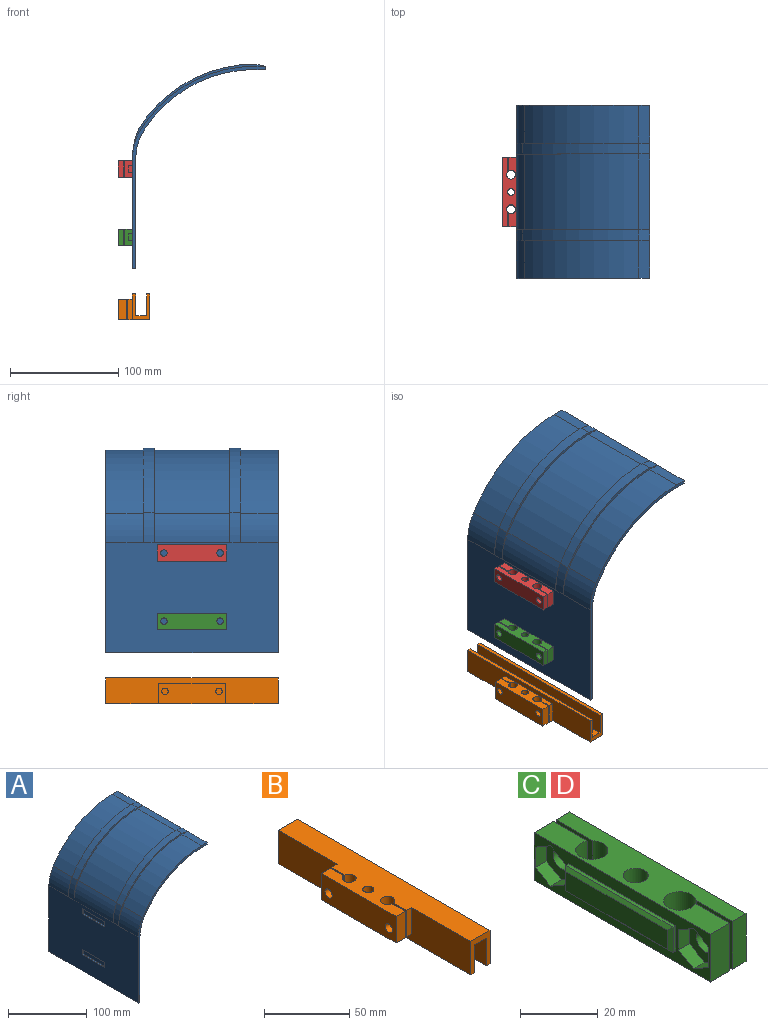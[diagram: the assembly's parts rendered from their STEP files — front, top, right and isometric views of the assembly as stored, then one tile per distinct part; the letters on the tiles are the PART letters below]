
ASSEMBLY  parts=4 mates=3
PART A: 38 faces, bbox 123.2x160x189.2 mm
  f0: plane 160x102.1mm, normal (-1,0,0), area 15695.5mm2, adj f3,f6,f12,f14,f15,f16,f20,f23
  f1: plane 35x10mm, normal (0,0,1), area 350mm2, adj f2,f9,f14,f27
  f2: cylinder r=124.43mm len=105.62mm, axis (0,1,0), area 4415.4mm2, adj f1,f3,f14,f27
  f3: cylinder r=50mm len=35mm, axis (0,1,0), area 974.6mm2, adj f0,f2,f14,f27
  f4: plane 35x10mm, normal (0,0,1), area 350mm2, adj f5,f9,f15,f22
  f5: cylinder r=124.43mm len=105.62mm, axis (0,1,0), area 4415.4mm2, adj f4,f6,f15,f22
  f6: cylinder r=50mm len=35mm, axis (0,1,0), area 974.6mm2, adj f0,f5,f15,f22
  f7: cylinder r=121.43mm len=160mm, axis (0,1,0), area 19466.7mm2, adj f8,f14,f15,f17
  f8: plane 160x10mm, normal (0,0,-1), area 1600mm2, adj f7,f9,f14,f15
  f9: plane 160x3mm, normal (1,0,0), area 480mm2, adj f1,f4,f8,f10,f14,f15,f18,f25
  f10: plane 70x10mm, normal (0,0,1), area 700mm2, adj f9,f11,f21,f26
  f11: cylinder r=124.43mm len=105.62mm, axis (0,1,0), area 8830.7mm2, adj f10,f16,f21,f26
  f12: plane 160x3mm, normal (0,0,-1), area 480mm2, adj f0,f13,f14,f15
  f13: plane 160x101.23mm, normal (1,0,0), area 16196.7mm2, adj f12,f14,f15,f17
  f14: plane 187.18x123.18mm, normal (0,-1,0), area 793.5mm2, adj f0,f1,f2,f3,f7,f8,f9,f12
  f15: plane 187.18x123.18mm, normal (0,1,0), area 793.5mm2, adj f0,f4,f5,f6,f7,f8,f9,f12
  f16: cylinder r=50mm len=70mm, axis (0,1,0), area 1949.3mm2, adj f0,f11,f21,f26
  f17: cylinder r=50mm len=160mm, axis (0,1,0), area 4550.7mm2, adj f7,f13,f14,f15
  f18: plane 10x10mm, normal (0.2,0,0.98), area 102mm2, adj f9,f19,f21,f22
  f19: cylinder r=126.43mm len=107.29mm, axis (0,1,0), area 1281.2mm2, adj f18,f20,f21,f22
  f20: cylinder r=67.31mm len=27.54mm, axis (0,1,0), area 283.7mm2, adj f0,f19,f21,f22
  f21: plane 123.18x87.09mm, normal (0,-1,0), area 283.1mm2, adj f10,f11,f16,f18,f19,f20
  f22: plane 123.18x87.09mm, normal (0,1,0), area 283.1mm2, adj f4,f5,f6,f18,f19,f20
  f23: cylinder r=67.31mm len=27.54mm, axis (0,-1,0), area 283.7mm2, adj f0,f24,f26,f27
  f24: cylinder r=126.43mm len=107.29mm, axis (0,-1,0), area 1281.2mm2, adj f23,f25,f26,f27
  f25: plane 10x10mm, normal (0.2,0,0.98), area 102mm2, adj f9,f24,f26,f27
  f26: plane 123.18x87.09mm, normal (0,1,0), area 283.1mm2, adj f10,f11,f16,f23,f24,f25
  f27: plane 123.18x87.09mm, normal (0,-1,0), area 283.1mm2, adj f1,f2,f3,f23,f24,f25
  f28: plane 40x2mm, normal (0,0,-1), area 80mm2, adj f0,f29,f31,f32
  f29: plane 8x2mm, normal (0,-1,0), area 16mm2, adj f0,f28,f30,f32
  f30: plane 40x2mm, normal (0,0,1), area 80mm2, adj f0,f29,f31,f32
  f31: plane 8x2mm, normal (0,1,0), area 16mm2, adj f0,f28,f30,f32
  f32: plane 40x8mm, normal (-1,0,0), area 320mm2, adj f28,f29,f30,f31
  f33: plane 8x2mm, normal (0,-1,0), area 16mm2, adj f0,f34,f36,f37
  f34: plane 40x2mm, normal (0,0,1), area 80mm2, adj f0,f33,f35,f37
  f35: plane 8x2mm, normal (0,1,0), area 16mm2, adj f0,f34,f36,f37
  f36: plane 40x2mm, normal (0,0,-1), area 80mm2, adj f0,f33,f35,f37
  f37: plane 40x8mm, normal (-1,0,0), area 320mm2, adj f33,f34,f35,f36
PART B: 27 faces, bbox 29x160x24 mm
  f0: plane 160x20mm, normal (1,0,0), area 3143.5mm2, adj f2,f12,f18,f19,f20,f25
  f1: plane 19x4.5mm, normal (0,-1,0), area 85.5mm2, adj f6,f15,f21,f22
  f2: cylinder r=3mm len=7.5mm, axis (-1,0,0), area 141.4mm2, adj f0,f15
  f3: plane 19x4.5mm, normal (0,1,0), area 85.5mm2, adj f6,f14,f21,f22
  f4: cylinder r=3mm len=7.5mm, axis (-1,0,0), area 141.4mm2, adj f5,f13
  f5: plane 62x19mm, normal (-1,0,0), area 1121.5mm2, adj f4,f6,f7,f8,f11,f21
  f6: plane 62x13mm, normal (0,0,-1), area 642.9mm2, adj f1,f3,f5,f7,f8,f9,f10,f13
  f7: plane 19x7.5mm, normal (0,-1,0), area 142.5mm2, adj f5,f6,f16,f21
  f8: plane 19x7.5mm, normal (0,1,0), area 142.5mm2, adj f5,f6,f13,f21
  f9: cylinder r=4.15mm len=19mm, axis (0,0,1), area 476.4mm2, adj f6,f15,f16,f21
  f10: cylinder r=4.15mm len=19mm, axis (0,0,1), area 476.4mm2, adj f6,f13,f14,f21
  f11: cylinder r=3mm len=7.5mm, axis (-1,0,0), area 141.4mm2, adj f5,f16
  f12: cylinder r=3mm len=7.5mm, axis (-1,0,0), area 141.4mm2, adj f0,f14
  f13: plane 19x10.88mm, normal (1,0,0), area 178.5mm2, adj f4,f6,f8,f10,f21
  f14: plane 19x10.88mm, normal (-1,0,0), area 178.5mm2, adj f3,f6,f10,f12,f21
  f15: plane 19x10.88mm, normal (-1,0,0), area 178.5mm2, adj f1,f2,f6,f9,f21
  f16: plane 19x10.88mm, normal (1,0,0), area 178.5mm2, adj f6,f7,f9,f11,f21
  f17: cylinder r=3.25mm len=19mm, axis (0,0,1), area 388mm2, adj f6,f21
  f18: plane 160x10mm, normal (0,0,-1), area 1600mm2, adj f0,f19,f20,f24
  f19: plane 24x16mm, normal (0,-1,0), area 184mm2, adj f0,f18,f21,f22,f23,f24,f25,f26
  f20: plane 24x16mm, normal (0,1,0), area 184mm2, adj f0,f18,f21,f22,f23,f24,f25,f26
  f21: plane 160x29mm, normal (0,0,1), area 3202.9mm2, adj f1,f3,f5,f7,f8,f9,f10,f13
  f22: plane 160x24mm, normal (-1,0,0), area 2662mm2, adj f1,f3,f6,f19,f20,f21,f25
  f23: plane 160x24mm, normal (1,0,0), area 3840mm2, adj f19,f20,f21,f26
  f24: plane 160x20mm, normal (-1,0,0), area 3200mm2, adj f18,f19,f20,f26
  f25: plane 160x3mm, normal (0,0,-1), area 480mm2, adj f0,f19,f20,f22
  f26: plane 160x3mm, normal (0,0,-1), area 480mm2, adj f19,f20,f23,f24
PART C: 42 faces, bbox 15x64x15 mm
  f0: plane 39x1mm, normal (0,0,-1), area 39mm2, adj f1,f3,f22,f41
  f1: plane 8x1mm, normal (0,-1,0), area 8mm2, adj f0,f2,f22,f40
  f2: plane 39x1mm, normal (0,0,1), area 39mm2, adj f1,f3,f22,f38
  f3: plane 8x1mm, normal (0,1,0), area 8mm2, adj f0,f2,f22,f39
  f4: cylinder r=3mm len=6mm, axis (-1,0,0), area 57.6mm2, adj f16,f30
  f5: cylinder r=3mm len=6mm, axis (-1,0,0), area 57.6mm2, adj f18,f29
  f6: plane 15x7.06mm, normal (0,1,0), area 105.9mm2, adj f8,f12,f16,f22
  f7: plane 15x7.06mm, normal (0,-1,0), area 105.9mm2, adj f8,f12,f18,f22
  f8: plane 64x13mm, normal (0,0,1), area 665.1mm2, adj f6,f7,f10,f11,f13,f15,f16,f17
  f9: cylinder r=3mm len=6mm, axis (-1,0,0), area 93.2mm2, adj f11,f17
  f10: cylinder r=4.15mm len=15mm, axis (0,0,1), area 371.9mm2, adj f8,f12,f15,f16
  f11: plane 64x15mm, normal (1,0,0), area 903.5mm2, adj f8,f9,f12,f14,f20,f21
  f12: plane 64x13mm, normal (0,0,-1), area 665.1mm2, adj f6,f7,f10,f11,f13,f15,f16,f17
  f13: cylinder r=4.15mm len=15mm, axis (0,0,1), area 371.9mm2, adj f8,f12,f17,f18
  f14: cylinder r=3mm len=6mm, axis (-1,0,0), area 93.2mm2, adj f11,f15
  f15: plane 15x13.19mm, normal (-1,0,0), area 169.6mm2, adj f8,f10,f12,f14,f20
  f16: plane 15x12.4mm, normal (1,0,0), area 157.7mm2, adj f4,f6,f8,f10,f12
  f17: plane 15x13.19mm, normal (-1,0,0), area 169.6mm2, adj f8,f9,f12,f13,f21
  f18: plane 15x12.4mm, normal (1,0,0), area 157.7mm2, adj f5,f7,f8,f12,f13
  f19: cylinder r=3.25mm len=15mm, axis (0,0,1), area 306.3mm2, adj f8,f12
  f20: plane 15x4.94mm, normal (0,1,0), area 74.1mm2, adj f8,f11,f12,f15
  f21: plane 15x4.94mm, normal (0,-1,0), area 74.1mm2, adj f8,f11,f12,f17
  f22: plane 64x15mm, normal (-1,0,0), area 438.4mm2, adj f0,f1,f2,f3,f6,f7,f8,f12
  f23: plane 5.5x4mm, normal (0,0.5,-0.87), area 25.4mm2, adj f22,f24,f28,f29
  f24: plane 5.5x4mm, normal (0,-0.5,-0.87), area 25.4mm2, adj f22,f23,f25,f29
  f25: plane 6.35x4mm, normal (0,-1,0), area 25.4mm2, adj f22,f24,f26,f29
  f26: plane 5.5x4mm, normal (0,-0.5,0.87), area 25.4mm2, adj f22,f25,f27,f29
  f27: plane 5.5x4mm, normal (0,0.5,0.87), area 25.4mm2, adj f22,f26,f28,f29
  f28: plane 6.35x4mm, normal (0,1,0), area 25.4mm2, adj f22,f23,f27,f29
  f29: plane 12.7x11mm, normal (-1,0,0), area 76.5mm2, adj f5,f23,f24,f25,f26,f27,f28
  f30: plane 12.7x11mm, normal (-1,0,0), area 76.5mm2, adj f4,f31,f32,f33,f34,f35,f36
  f31: plane 5.5x4mm, normal (0,0.5,-0.87), area 25.4mm2, adj f22,f30,f32,f36
  f32: plane 5.5x4mm, normal (0,-0.5,-0.87), area 25.4mm2, adj f22,f30,f31,f33
  f33: plane 6.35x4mm, normal (0,-1,0), area 25.4mm2, adj f22,f30,f32,f34
  f34: plane 5.5x4mm, normal (0,-0.5,0.87), area 25.4mm2, adj f22,f30,f33,f35
  f35: plane 5.5x4mm, normal (0,0.5,0.87), area 25.4mm2, adj f22,f30,f34,f36
  f36: plane 6.35x4mm, normal (0,1,0), area 25.4mm2, adj f22,f30,f31,f35
  f37: plane 37x6mm, normal (-1,0,0), area 222mm2, adj f38,f39,f40,f41
  f38: plane 39x1mm, normal (-0.71,0,0.71), area 53.7mm2, adj f2,f37,f39,f40
  f39: plane 8x1mm, normal (-0.71,0.71,0), area 9.9mm2, adj f3,f37,f38,f41
  f40: plane 8x1mm, normal (-0.71,-0.71,0), area 9.9mm2, adj f1,f37,f38,f41
  f41: plane 39x1mm, normal (-0.71,0,-0.71), area 53.7mm2, adj f0,f37,f39,f40
PART D: same geometry as C
PLACE A t=(-51.94,90.72,100.82)mm
PLACE B rot(axis=(1,0,0),180deg) t=(-61.94,10.72,-118.54)mm
PLACE C rot(axis=(0,1,0),180deg) t=(-61.94,10.72,-53.54)mm
PLACE D rot(axis=(0,1,0),180deg) t=(-61.94,10.72,9.56)mm
MATE fastened D.f37 <-> A.f37  axis (1,0,0) through (-54.94,10.72,9.56)mm
MATE fastened B.f17 <-> C.f19  axis (0,0,1) through (-61.94,10.72,-111.04)mm
MATE fastened C.f37 <-> A.f32  axis (1,0,0) through (-54.94,10.72,-53.54)mm
